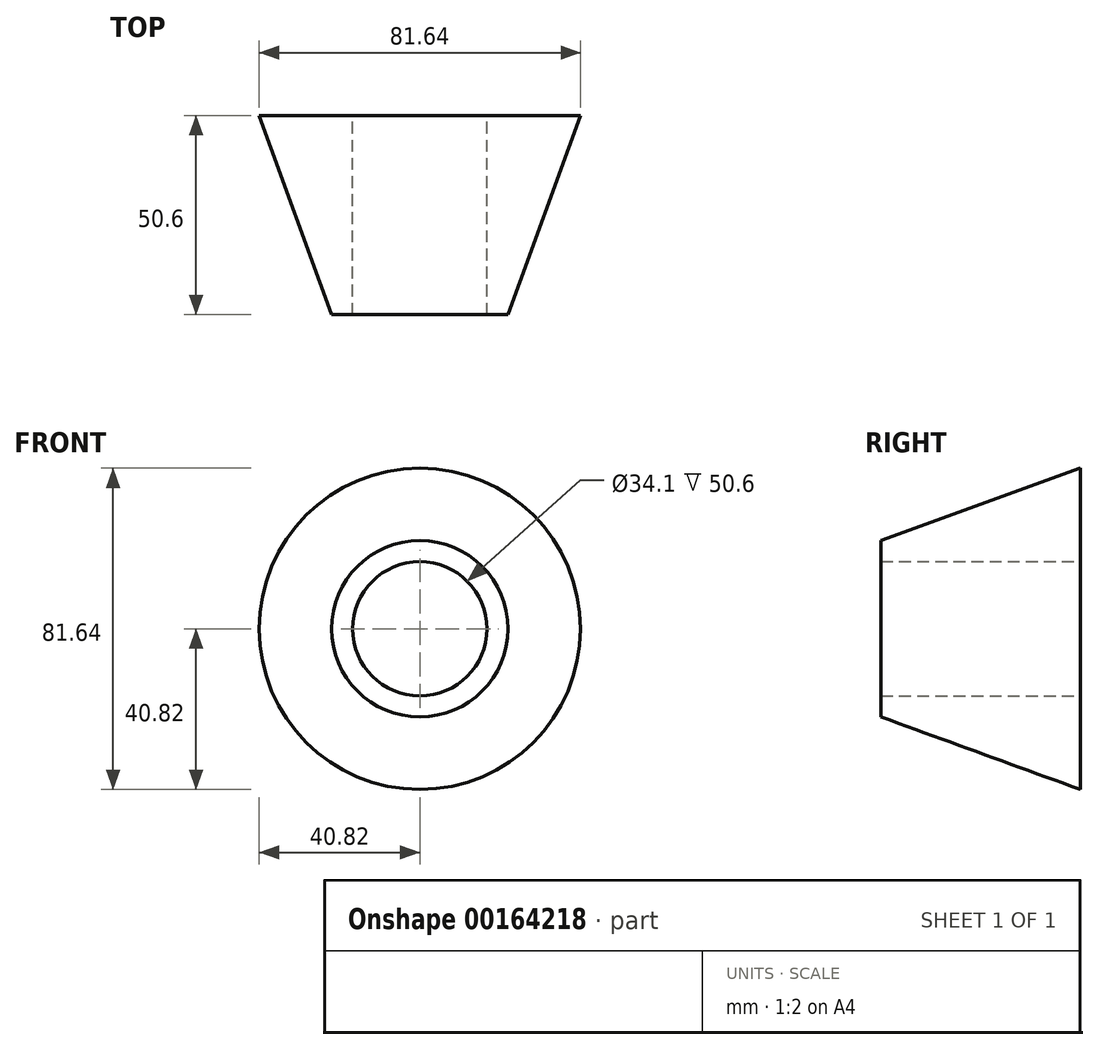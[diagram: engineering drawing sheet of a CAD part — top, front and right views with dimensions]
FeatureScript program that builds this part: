
annotation { "Feature Type Name" : "Feature", "Feature Type Description" : "" }
export const myFeature = defineFeature(function(context is Context, id is Id, definition is map)
    precondition{}
    {
        {
            var Q0;
            Q0=qCreatedBy(makeId("Front.planeOp"),FACE);
            var sketch = newSketch(context, id + "F0", { "sketchPlane" : qUnion([Q0])});
            skCircle(sketch, "E0", {"center": v(0, 0) * mm, "radius": 40.82 * mm});
            skSolve(sketch);
        }
        {
            var Q0;
            Q0 = qSketchRegion(id + "F0", true);
            extrude(context, id + "F1", {"entities" : qUnion([Q0]), "depth" : 50.6 * mm, "hasDraft" : true, "draftAngle" : 20 * degree, "draftPullDirection" : true});
        }
        {
            var Q0;
            Q0=makeQuery(id+"F1.opExtrude","CAP_FACE",FACE,{"disambiguationData":[OSD([sQuery(id+"F0.wireOp",EDGE,"E0")])],"isStart":true});
            var sketch = newSketch(context, id + "F2", { "sketchPlane" : qUnion([Q0])});
            skCircle(sketch, "E1", {"center": v(0, 0) * mm, "radius": 17.05 * mm});
            skSolve(sketch);
        }
        {
            var Q0;
            Q0=makeQuery(id+"F2.imprint","IMPRINT",FACE,{"disambiguationData":[TD([[makeQuery(id+"F2.imprint","IMPRINT",EDGE,{"derivedFrom":sQuery(id+"F2.wireOp",EDGE,"E1")}),1.0]])]});
            extrude(context, id + "F3", {"entities" : qUnion([Q0]), "operationType" : NewBodyOperationType.REMOVE, "endBound" : BoundingType.THROUGH_ALL, "oppositeDirection" : true, "depth" : 25 * mm});
        }
    });
